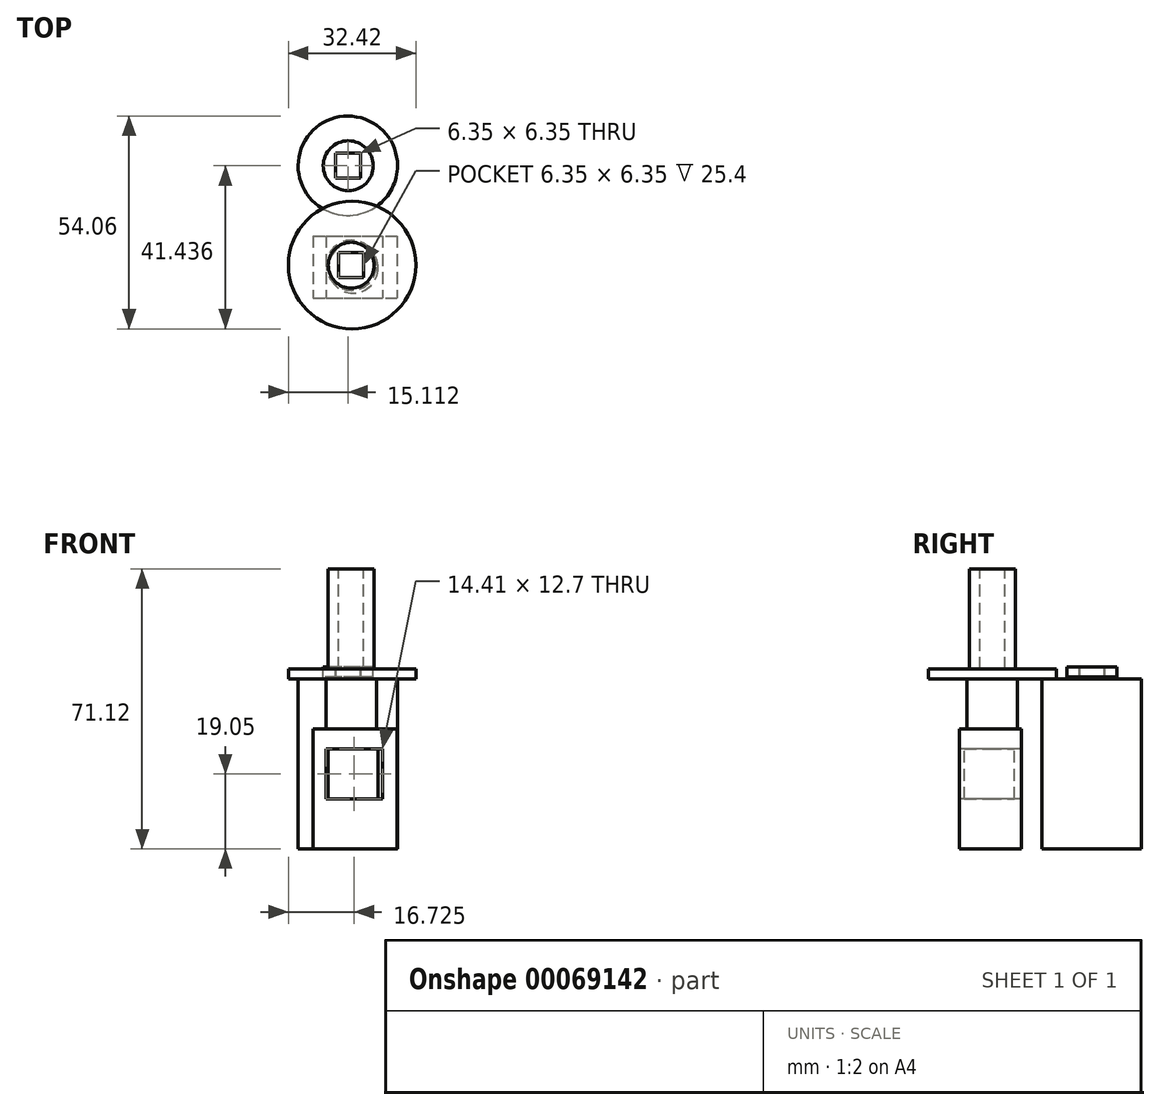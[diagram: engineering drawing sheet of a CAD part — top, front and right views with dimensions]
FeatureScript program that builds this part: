
annotation { "Feature Type Name" : "Feature", "Feature Type Description" : "" }
export const myFeature = defineFeature(function(context is Context, id is Id, definition is map)
    precondition{}
    {
        {
            var Q0;
            Q0=qCreatedBy(makeId("Top.planeOp"),FACE);
            var sketch = newSketch(context, id + "F0", { "sketchPlane" : qUnion([Q0])});
            skCircle(sketch, "E0", {"center": v(-6.39, 32.76) * mm, "radius": 12.62 * mm});
            skCircle(sketch, "E1", {"center": v(-5.5, 7.46) * mm, "radius": 4.23 * mm});
            skSolve(sketch);
        }
        {
            var Q0;
            Q0=makeQuery(id+"F0.imprint","IMPRINT",FACE,{"disambiguationData":[TD([[makeQuery(id+"F0.imprint","IMPRINT",EDGE,{"derivedFrom":sQuery(id+"F0.wireOp",EDGE,"E0")}),1.0]])]});
            var Q1;
            Q1=makeQuery(id+"F0.imprint","IMPRINT",FACE,{"disambiguationData":[TD([[makeQuery(id+"F0.imprint","IMPRINT",EDGE,{"derivedFrom":sQuery(id+"F0.wireOp",EDGE,"E1")}),1.0]])]});
            extrude(context, id + "F1", {"entities" : qUnion([Q0, Q1]), "depth" : 17.78 * mm});
        }
        {
            var Q0;
            Q0=makeQuery(id+"F1.opExtrude","CAP_FACE",FACE,{"disambiguationData":[OSD([sQuery(id+"F0.wireOp",EDGE,"E1")])],"isStart":false});
            var sketch = newSketch(context, id + "F2", { "sketchPlane" : qUnion([Q0])});
            skCircle(sketch, "E2", {"center": v(-5.5, 7.46) * mm, "radius": 6.38 * mm});
            skSolve(sketch);
        }
        {
            var Q0;
            Q0=makeQuery(id+"F2.imprint","IMPRINT",FACE,{"disambiguationData":[TD([[makeQuery(id+"F2.imprint","IMPRINT",EDGE,{"derivedFrom":sQuery(id+"F2.wireOp",EDGE,"E2")}),1.0]])]});
            extrude(context, id + "F3", {"entities" : qUnion([Q0]), "operationType" : NewBodyOperationType.ADD, "oppositeDirection" : true, "depth" : 12.7 * mm});
        }
        {
            var Q0;
            Q0=qCreatedBy(makeId("Top.planeOp"),FACE);
            var sketch = newSketch(context, id + "F4", { "sketchPlane" : qUnion([Q0])});
            skLineSegment(sketch, "E3.bottom", {"start": v(-15.2, 14.91) * mm, "end": v(6.05, 14.91) * mm});
            skLineSegment(sketch, "E3.top", {"start": v(-15.2, -0.84) * mm, "end": v(6.05, -0.84) * mm});
            skLineSegment(sketch, "E3.left", {"start": v(-15.2, 14.91) * mm, "end": v(-15.2, -0.84) * mm});
            skLineSegment(sketch, "E3.right", {"start": v(6.05, 14.91) * mm, "end": v(6.05, -0.84) * mm});
            skSolve(sketch);
        }
        {
            var Q0;
            Q0=makeQuery(id+"F4.imprint","IMPRINT",FACE,{"disambiguationData":[TD([[makeQuery(id+"F4.imprint","IMPRINT",EDGE,{"derivedFrom":sQuery(id+"F4.wireOp",EDGE,"E3.bottom")}),-1.0]])]});
            extrude(context, id + "F5", {"entities" : qUnion([Q0]), "operationType" : NewBodyOperationType.ADD, "depth" : 5.08 * mm});
        }
        {
            var Q0;
            {var subQ0=sQuery(id+"F0.wireOp",EDGE,"E1");Q0=makeQuery(id+"F3.boolean.opBoolean","MERGE",FACE,{"derivedFrom":[makeQuery(id+"F1.opExtrude","CAP_FACE",FACE,{"disambiguationData":[OSD([subQ0])],"isStart":false}),makeQuery(id+"F3.opExtrude","CAP_FACE",FACE,{"disambiguationData":[OSD([subQ0,sQuery(id+"F2.wireOp",EDGE,"E2")])],"isStart":true})]});}
            var sketch = newSketch(context, id + "F6", { "sketchPlane" : qUnion([Q0])});
            skLineSegment(sketch, "E4.bottom", {"start": v(-8.7, 10.66) * mm, "end": v(-2.36, 10.66) * mm});
            skLineSegment(sketch, "E4.top", {"start": v(-8.7, 4.31) * mm, "end": v(-2.36, 4.31) * mm});
            skLineSegment(sketch, "E4.left", {"start": v(-8.7, 10.66) * mm, "end": v(-8.7, 4.31) * mm});
            skLineSegment(sketch, "E4.right", {"start": v(-2.36, 10.66) * mm, "end": v(-2.36, 4.31) * mm});
            skSolve(sketch);
        }
        {
            var Q0;
            Q0=makeQuery(id+"F6.imprint","IMPRINT",FACE,{"disambiguationData":[TD([[makeQuery(id+"F6.imprint","IMPRINT",EDGE,{"derivedFrom":sQuery(id+"F6.wireOp",EDGE,"E4.bottom")}),-1.0]])]});
            extrude(context, id + "F7", {"entities" : qUnion([Q0]), "operationType" : NewBodyOperationType.ADD, "depth" : 2.54 * mm});
        }
        {
            var Q0;
            Q0=makeQuery(id+"F1.opExtrude","CAP_FACE",FACE,{"disambiguationData":[OSD([sQuery(id+"F0.wireOp",EDGE,"E0")])],"isStart":false});
            var sketch = newSketch(context, id + "F8", { "sketchPlane" : qUnion([Q0])});
            skLineSegment(sketch, "E5.bottom", {"start": v(-3.21, 35.93) * mm, "end": v(-9.56, 35.93) * mm});
            skLineSegment(sketch, "E5.top", {"start": v(-3.21, 29.58) * mm, "end": v(-9.56, 29.58) * mm});
            skLineSegment(sketch, "E5.left", {"start": v(-3.21, 35.93) * mm, "end": v(-3.21, 29.58) * mm});
            skLineSegment(sketch, "E5.right", {"start": v(-9.56, 35.93) * mm, "end": v(-9.56, 29.58) * mm});
            skSolve(sketch);
        }
        {
            var Q0;
            Q0=makeQuery(id+"F8.imprint","IMPRINT",FACE,{"disambiguationData":[TD([[makeQuery(id+"F8.imprint","IMPRINT",EDGE,{"derivedFrom":sQuery(id+"F8.wireOp",EDGE,"E5.bottom")}),1.0]])]});
            extrude(context, id + "F9", {"entities" : qUnion([Q0]), "operationType" : NewBodyOperationType.ADD, "depth" : 3.05 * mm});
        }
        {
            var Q0;
            Q0=makeQuery(id+"F7.opExtrude","CAP_FACE",FACE,{"disambiguationData":[OSD([sQuery(id+"F6.wireOp",EDGE,"E4.bottom"),sQuery(id+"F6.wireOp",EDGE,"E4.top"),sQuery(id+"F6.wireOp",EDGE,"E4.left"),sQuery(id+"F6.wireOp",EDGE,"E4.right")])],"isStart":false});
            var sketch = newSketch(context, id + "F10", { "sketchPlane" : qUnion([Q0])});
            skCircle(sketch, "E6", {"center": v(-5.29, 7.53) * mm, "radius": 16.21 * mm});
            skCircle(sketch, "E7", {"center": v(-6.54, 32.86) * mm, "radius": 6.1 * mm});
            skSolve(sketch);
        }
        {
            var Q0;
            Q0=makeQuery(id+"F10.imprint","IMPRINT",FACE,{"disambiguationData":[TD([[makeQuery(id+"F10.imprint","IMPRINT",EDGE,{"derivedFrom":sQuery(id+"F10.wireOp",EDGE,"E6")}),1.0]])]});
            extrude(context, id + "F11", {"entities" : qUnion([Q0]), "oppositeDirection" : true, "depth" : 2.54 * mm});
        }
        {
            var Q0;
            Q0=makeQuery(id+"F9.opExtrude","CAP_FACE",FACE,{"disambiguationData":[OSD([sQuery(id+"F8.wireOp",EDGE,"E5.bottom"),sQuery(id+"F8.wireOp",EDGE,"E5.top"),sQuery(id+"F8.wireOp",EDGE,"E5.left"),sQuery(id+"F8.wireOp",EDGE,"E5.right")])],"isStart":false});
            var sketch = newSketch(context, id + "F12", { "sketchPlane" : qUnion([Q0])});
            skCircle(sketch, "E8", {"center": v(-6.28, 32.75) * mm, "radius": 6.35 * mm});
            skSolve(sketch);
        }
        {
            var Q0;
            Q0=makeQuery(id+"F12.imprint","IMPRINT",FACE,{"disambiguationData":[TD([[makeQuery(id+"F12.imprint","IMPRINT",EDGE,{"derivedFrom":sQuery(id+"F12.wireOp",EDGE,"E8")}),1.0]])]});
            extrude(context, id + "F13", {"entities" : qUnion([Q0]), "oppositeDirection" : true, "depth" : 2.54 * mm});
        }
        {
            var Q0;
            Q0=makeQuery(id+"F7.opExtrude","CAP_FACE",FACE,{"disambiguationData":[OSD([sQuery(id+"F6.wireOp",EDGE,"E4.bottom"),sQuery(id+"F6.wireOp",EDGE,"E4.top"),sQuery(id+"F6.wireOp",EDGE,"E4.left"),sQuery(id+"F6.wireOp",EDGE,"E4.right")])],"isStart":false});
            var sketch = newSketch(context, id + "F14", { "sketchPlane" : qUnion([Q0])});
            skCircle(sketch, "E9", {"center": v(-5.53, 7.49) * mm, "radius": 5.82 * mm});
            skSolve(sketch);
        }
        {
            var Q0;
            Q0=makeQuery(id+"F14.imprint","IMPRINT",FACE,{"disambiguationData":[TD([[makeQuery(id+"F14.imprint","IMPRINT",EDGE,{"derivedFrom":sQuery(id+"F14.wireOp",EDGE,"E9")}),1.0]])]});
            extrude(context, id + "F15", {"entities" : qUnion([Q0]), "operationType" : NewBodyOperationType.ADD, "depth" : 25.4 * mm});
        }
        {
            var Q0;
            Q0=makeQuery(id+"F7.opExtrude","CAP_FACE",FACE,{"disambiguationData":[OSD([sQuery(id+"F6.wireOp",EDGE,"E4.bottom"),sQuery(id+"F6.wireOp",EDGE,"E4.top"),sQuery(id+"F6.wireOp",EDGE,"E4.left"),sQuery(id+"F6.wireOp",EDGE,"E4.right")])],"isStart":false});
            extrude(context, id + "F16", {"entities" : qUnion([Q0]), "depth" : 25.4 * mm});
        }
        {
            var Q0;
            Q0=makeQuery(id+"F1.opExtrude","CAP_FACE",FACE,{"disambiguationData":[OSD([sQuery(id+"F0.wireOp",EDGE,"E0")])],"isStart":true});
            extrude(context, id + "F17", {"entities" : qUnion([Q0]), "operationType" : NewBodyOperationType.ADD, "depth" : 19.05 * mm});
        }
        {
            var Q0;
            Q0=makeQuery(id+"F5.boolean.opBoolean","MERGE",FACE,{"derivedFrom":[makeQuery(id+"F1.opExtrude","CAP_FACE",FACE,{"disambiguationData":[OSD([sQuery(id+"F0.wireOp",EDGE,"E1")])],"isStart":true}),makeQuery(id+"F5.opExtrude","CAP_FACE",FACE,{"disambiguationData":[OSD([sQuery(id+"F4.wireOp",EDGE,"E3.bottom"),sQuery(id+"F4.wireOp",EDGE,"E3.top"),sQuery(id+"F4.wireOp",EDGE,"E3.left"),sQuery(id+"F4.wireOp",EDGE,"E3.right")])],"isStart":true})]});
            var sketch = newSketch(context, id + "F18", { "sketchPlane" : qUnion([Q0])});
            skCircle(sketch, "E10", {"center": v(-5.03, -6.78) * mm, "radius": 6.35 * mm});
            skSolve(sketch);
        }
        {
            var Q0;
            Q0=makeQuery(id+"F18.imprint","IMPRINT",FACE,{"disambiguationData":[TD([[makeQuery(id+"F18.imprint","IMPRINT",EDGE,{"derivedFrom":sQuery(id+"F18.wireOp",EDGE,"E10")}),1.0]])]});
            extrude(context, id + "F19", {"entities" : qUnion([Q0]), "operationType" : NewBodyOperationType.ADD, "depth" : 12.7 * mm});
        }
        {
            var Q0;
            Q0=makeQuery(id+"F5.boolean.opBoolean","MERGE",FACE,{"derivedFrom":[makeQuery(id+"F1.opExtrude","CAP_FACE",FACE,{"disambiguationData":[OSD([sQuery(id+"F0.wireOp",EDGE,"E1")])],"isStart":true}),makeQuery(id+"F5.opExtrude","CAP_FACE",FACE,{"disambiguationData":[OSD([sQuery(id+"F4.wireOp",EDGE,"E3.bottom"),sQuery(id+"F4.wireOp",EDGE,"E3.top"),sQuery(id+"F4.wireOp",EDGE,"E3.left"),sQuery(id+"F4.wireOp",EDGE,"E3.right")])],"isStart":true})]});
            var sketch = newSketch(context, id + "F20", { "sketchPlane" : qUnion([Q0])});
            skLineSegment(sketch, "E11.bottom", {"start": v(-15.2, -14.91) * mm, "end": v(-11.98, -14.91) * mm});
            skLineSegment(sketch, "E11.top", {"start": v(-15.2, 0.84) * mm, "end": v(-11.98, 0.84) * mm});
            skLineSegment(sketch, "E11.left", {"start": v(-15.2, -14.91) * mm, "end": v(-15.2, 0.84) * mm});
            skLineSegment(sketch, "E11.right", {"start": v(-11.98, -14.91) * mm, "end": v(-11.98, 0.84) * mm});
            skLineSegment(sketch, "E12.bottom", {"start": v(6.05, -14.91) * mm, "end": v(2.43, -14.91) * mm});
            skLineSegment(sketch, "E12.top", {"start": v(6.05, 0.84) * mm, "end": v(2.43, 0.84) * mm});
            skLineSegment(sketch, "E12.left", {"start": v(6.05, -14.91) * mm, "end": v(6.05, 0.84) * mm});
            skLineSegment(sketch, "E12.right", {"start": v(2.43, -14.91) * mm, "end": v(2.43, 0.84) * mm});
            skSolve(sketch);
        }
        {
            var Q0;
            Q0=makeQuery(id+"F20.imprint","IMPRINT",FACE,{"disambiguationData":[TD([[makeQuery(id+"F20.imprint","IMPRINT",EDGE,{"derivedFrom":sQuery(id+"F20.wireOp",EDGE,"E12.bottom")}),1.0]])]});
            var Q1;
            Q1=makeQuery(id+"F20.imprint","IMPRINT",FACE,{"disambiguationData":[TD([[makeQuery(id+"F20.imprint","IMPRINT",EDGE,{"derivedFrom":sQuery(id+"F20.wireOp",EDGE,"E11.bottom")}),1.0]])]});
            extrude(context, id + "F21", {"entities" : qUnion([Q0, Q1]), "operationType" : NewBodyOperationType.ADD, "depth" : 25.4 * mm});
        }
        {
            var Q0;
            Q0=makeQuery(id+"F17.opExtrude","CAP_FACE",FACE,{"disambiguationData":[OSD([sQuery(id+"F0.wireOp",EDGE,"E0")])],"isStart":false});
            extrude(context, id + "F22", {"entities" : qUnion([Q0]), "operationType" : NewBodyOperationType.ADD, "depth" : 6.35 * mm});
        }
        {
            var Q0;
            Q0=makeQuery(id+"F21.opExtrude","SWEPT_FACE",FACE,{"disambiguationData":[OSD([sQuery(id+"F20.wireOp",EDGE,"E12.right")])]});
            var sketch = newSketch(context, id + "F23", { "sketchPlane" : qUnion([Q0])});
            skLineSegment(sketch, "E13.bottom", {"start": v(0.84, -12.7) * mm, "end": v(-14.91, -12.7) * mm});
            skLineSegment(sketch, "E13.top", {"start": v(0.84, -25.4) * mm, "end": v(-14.91, -25.4) * mm});
            skLineSegment(sketch, "E13.left", {"start": v(0.84, -12.7) * mm, "end": v(0.84, -25.4) * mm});
            skLineSegment(sketch, "E13.right", {"start": v(-14.91, -12.7) * mm, "end": v(-14.91, -25.4) * mm});
            skSolve(sketch);
        }
        {
            var Q0;
            Q0=makeQuery(id+"F23.imprint","IMPRINT",FACE,{"disambiguationData":[TD([[makeQuery(id+"F23.imprint","IMPRINT",EDGE,{"derivedFrom":sQuery(id+"F23.wireOp",EDGE,"E13.bottom")}),1.0]])]});
            extrude(context, id + "F24", {"entities" : qUnion([Q0]), "operationType" : NewBodyOperationType.ADD, "depth" : 15.24 * mm});
        }
    });
